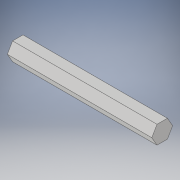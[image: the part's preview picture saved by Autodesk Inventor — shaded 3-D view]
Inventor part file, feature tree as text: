
AUTODESK INVENTOR PART (.ipt)
format: ipt  version: 2018 (Build 220112000, 112)  size: 95,232 bytes
history: native  units: in
note: dims shown in document units (in); Inventor stores cm internally (conversion verified against a paired STEP export)
features: extrude x1, sketch x1
ambient origin geometry x8: Origin, YZ Plane, XZ Plane, XY Plane, X Axis, Y Axis, Z Axis, Center Point
bodies: Solid1 (feature_tree)
feature tree (2):
  extrude  "Extrusion1"  Depth=4.0in TaperAngle=0.0deg
  sketch  "Sketch1"  dims[d0=0.25in d1=4.0in d2=0.0in]
